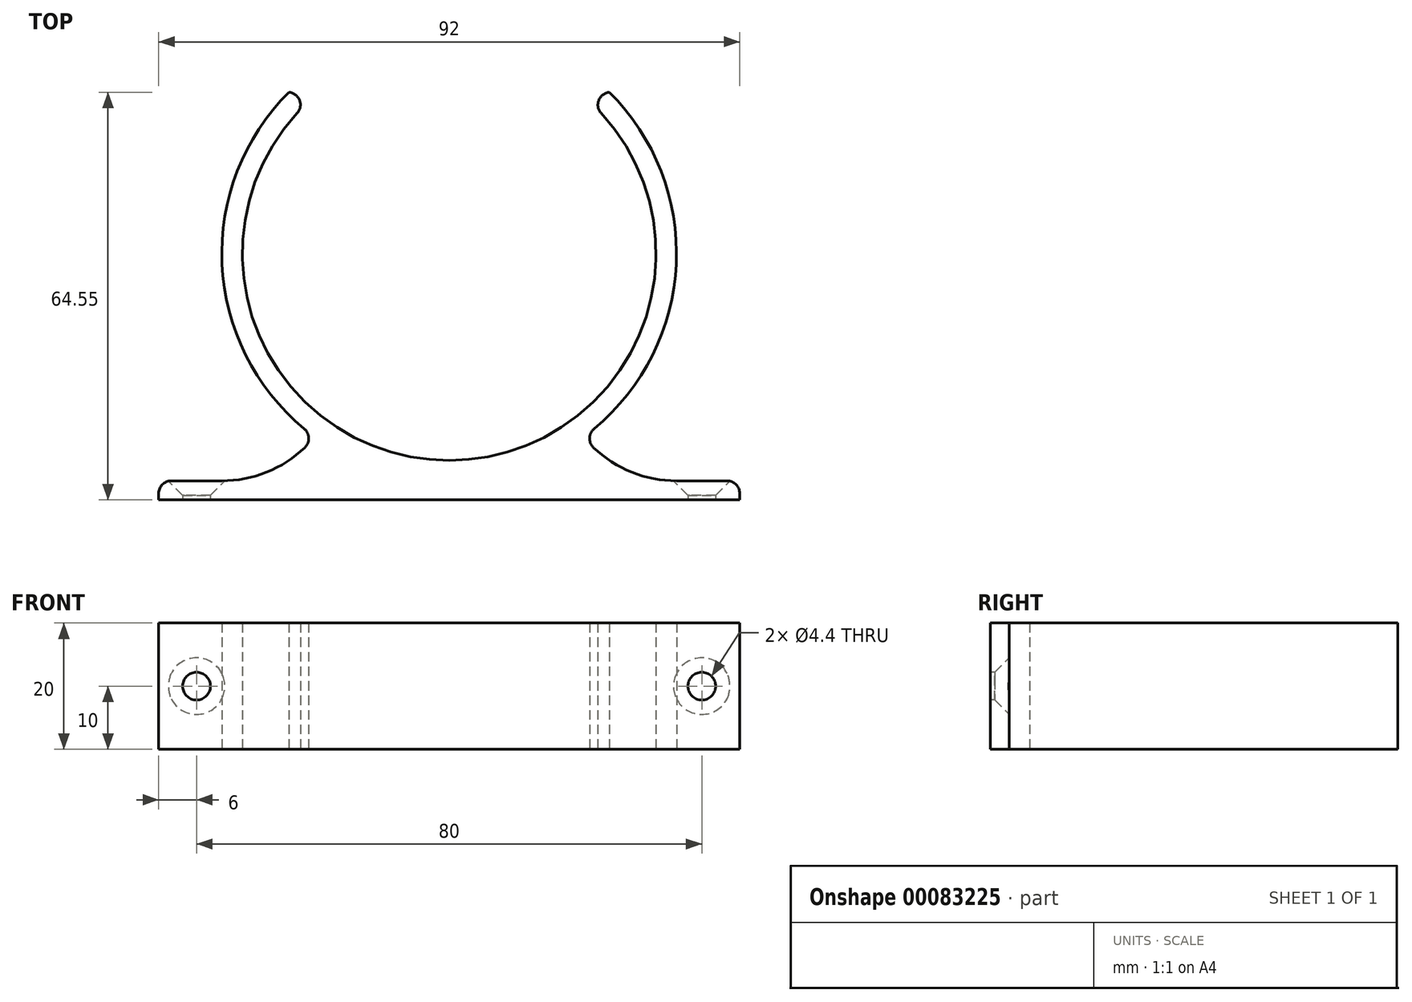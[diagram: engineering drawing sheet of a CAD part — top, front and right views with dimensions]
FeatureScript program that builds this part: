
annotation { "Feature Type Name" : "Feature", "Feature Type Description" : "" }
export const myFeature = defineFeature(function(context is Context, id is Id, definition is map)
    precondition{}
    {
        {
            assignVariable(context, id + "F0", {"name" : "h", "anyValue" : 20});
        }
        {
            var Q0;
            Q0=qCreatedBy(makeId("Top.planeOp"),FACE);
            var sketch = newSketch(context, id + "F1", { "sketchPlane" : qUnion([Q0])});
            skCircle(sketch, "E0", {"center": v(0, 0) * mm, "radius": 36 * mm});
            skCircle(sketch, "E1", {"center": v(0, 0) * mm, "radius": 32.75 * mm});
            skLineSegment(sketch, "E2", {"start": v(-36, 0) * mm, "end": v(36, 0) * mm, "construction": true});
            skLineSegment(sketch, "E3", {"start": v(36, 0) * mm, "end": v(36, -39) * mm});
            skLineSegment(sketch, "E4", {"start": v(36, -39) * mm, "end": v(-36, -39) * mm});
            skLineSegment(sketch, "E5", {"start": v(-36, -39) * mm, "end": v(-36, 0) * mm});
            skLineSegment(sketch, "E6", {"start": v(-36, -39) * mm, "end": v(-46, -39) * mm});
            skLineSegment(sketch, "E7", {"start": v(-46, -39) * mm, "end": v(-46, -36) * mm});
            skLineSegment(sketch, "E8", {"start": v(-46, -36) * mm, "end": v(-36, -36) * mm});
            skLineSegment(sketch, "E9", {"start": v(36, -39) * mm, "end": v(46, -39) * mm});
            skLineSegment(sketch, "E10", {"start": v(46, -39) * mm, "end": v(46, -36) * mm});
            skLineSegment(sketch, "E11", {"start": v(46, -36) * mm, "end": v(36, -36) * mm});
            skLineSegment(sketch, "E12", {"start": v(-36, -17.01) * mm, "end": v(36, -17.01) * mm, "construction": true});
            skCircle(sketch, "E13", {"center": v(-36, -17.01) * mm, "radius": 18.99 * mm});
            skCircle(sketch, "E14", {"center": v(36, -17.01) * mm, "radius": 18.99 * mm});
            skLineSegment(sketch, "E15", {"start": v(-25.37, 25.55) * mm, "end": v(25.37, 25.55) * mm, "construction": true});
            skLineSegment(sketch, "E16", {"start": v(-25.37, 25.55) * mm, "end": v(-20.5, 25.55) * mm});
            skLineSegment(sketch, "E17", {"start": v(25.37, 25.55) * mm, "end": v(20.5, 25.55) * mm});
            skSolve(sketch);
        }
        {
            var Q0;
            {var subQ0=sQuery(id+"F1.wireOp",EDGE,"E6");Q0=makeQuery(id+"F1.imprint","IMPRINT",FACE,{"disambiguationData":[TD([[makeQuery(id+"F1.imprint","IMPRINT",EDGE,{"derivedFrom":subQ0}),-1.0]])]});}
            var Q1;
            {var subQ1=sQuery(id+"F1.wireOp",EDGE,"E4");Q1=makeQuery(id+"F1.imprint","IMPRINT",FACE,{"disambiguationData":[TD([[makeQuery(id+"F1.imprint","IMPRINT",EDGE,{"derivedFrom":subQ1}),-1.0]])]});}
            var Q2;
            {var subQ0=sQuery(id+"F1.wireOp",EDGE,"E9");Q2=makeQuery(id+"F1.imprint","IMPRINT",FACE,{"disambiguationData":[TD([[makeQuery(id+"F1.imprint","IMPRINT",EDGE,{"derivedFrom":subQ0}),1.0]])]});}
            var Q3;
            {var subQ0=sQuery(id+"F1.wireOp",EDGE,"E13");var subQ1=sQuery(id+"F1.wireOp",EDGE,"E0");var subQ2=makeQuery(id+"F1.imprint","INTERSECT",VERTEX,{"disambiguationData":[OD(1.0)],"derivedFrom":[subQ1,subQ0]});Q3=makeQuery(id+"F1.imprint","IMPRINT",FACE,{"disambiguationData":[TD([[makeQuery(id+"F1.imprint","IMPRINT",EDGE,{"disambiguationData":[TD([[subQ2,-1.0]])],"derivedFrom":subQ1}),1.0]])]});}
            var Q4;
            {var subQ0=sQuery(id+"F1.wireOp",EDGE,"E14");var subQ1=sQuery(id+"F1.wireOp",EDGE,"E0");var subQ2=makeQuery(id+"F1.imprint","INTERSECT",VERTEX,{"disambiguationData":[OD(0.0)],"derivedFrom":[subQ1,subQ0]});Q4=makeQuery(id+"F1.imprint","IMPRINT",FACE,{"disambiguationData":[TD([[makeQuery(id+"F1.imprint","IMPRINT",EDGE,{"disambiguationData":[TD([[subQ2,-1.0]])],"derivedFrom":subQ1}),1.0]])]});}
            var Q5;
            {var subQ5=sQuery(id+"F1.wireOp",EDGE,"E0");var subQ6=makeQuery(id+"F1.imprint","INTERSECT",VERTEX,{"derivedFrom":[subQ5,sQuery(id+"F1.wireOp",EDGE,"E3")]});Q5=makeQuery(id+"F1.imprint","IMPRINT",FACE,{"disambiguationData":[TD([[makeQuery(id+"F1.imprint","IMPRINT",EDGE,{"disambiguationData":[TD([[subQ6,-1.0]])],"derivedFrom":subQ5}),1.0]])]});}
            var Q6;
            {var subQ0=sQuery(id+"F1.wireOp",EDGE,"E13");var subQ1=sQuery(id+"F1.wireOp",EDGE,"E0");var subQ2=makeQuery(id+"F1.imprint","INTERSECT",VERTEX,{"disambiguationData":[OD(0.0)],"derivedFrom":[subQ1,subQ0]});Q6=makeQuery(id+"F1.imprint","IMPRINT",FACE,{"disambiguationData":[TD([[makeQuery(id+"F1.imprint","IMPRINT",EDGE,{"disambiguationData":[TD([[subQ2,-1.0]])],"derivedFrom":subQ1}),1.0]])]});}
            var Q7;
            {var subQ5=sQuery(id+"F1.wireOp",EDGE,"E16");Q7=makeQuery(id+"F1.imprint","IMPRINT",FACE,{"disambiguationData":[TD([[makeQuery(id+"F1.imprint","IMPRINT",EDGE,{"derivedFrom":subQ5}),-1.0]])]});}
            extrude(context, id + "F2", {"entities" : qUnion([Q0, Q1, Q2, Q3, Q4, Q5, Q6, Q7]), "depth" : (getVariable(context, 'h')) * mm});
        }
        {
            var Q0;
            Q0=makeQuery(id+"F2.opExtrude","SWEPT_EDGE",EDGE,{"disambiguationData":[OSD([sQuery(id+"F1.wireOp",EDGE,"E1"),sQuery(id+"F1.wireOp",EDGE,"E17")])]});
            var Q1;
            Q1=makeQuery(id+"F2.opExtrude","SWEPT_EDGE",EDGE,{"disambiguationData":[OSD([sQuery(id+"F1.wireOp",EDGE,"E1"),sQuery(id+"F1.wireOp",EDGE,"E16")])]});
            var Q2;
            Q2=makeQuery(id+"F2.opExtrude","SWEPT_EDGE",EDGE,{"disambiguationData":[OSD([sQuery(id+"F1.wireOp",EDGE,"E0"),sQuery(id+"F1.wireOp",EDGE,"E13")])]});
            var Q3;
            Q3=makeQuery(id+"F2.opExtrude","SWEPT_EDGE",EDGE,{"disambiguationData":[OSD([sQuery(id+"F1.wireOp",EDGE,"E0"),sQuery(id+"F1.wireOp",EDGE,"E14")])]});
            var Q4;
            Q4=makeQuery(id+"F2.opExtrude","SWEPT_EDGE",EDGE,{"disambiguationData":[OSD([sQuery(id+"F1.wireOp",EDGE,"E10"),sQuery(id+"F1.wireOp",EDGE,"E11")])]});
            var Q5;
            Q5=makeQuery(id+"F2.opExtrude","SWEPT_EDGE",EDGE,{"disambiguationData":[OSD([sQuery(id+"F1.wireOp",EDGE,"E7"),sQuery(id+"F1.wireOp",EDGE,"E8")])]});
            fillet(context, id + "F3", {"entities" : qUnion([Q0, Q1, Q2, Q3, Q4, Q5]), "radius" : 2 * mm, "tangentPropagation" : true, "allowEdgeOverflow" : false});
        }
        {
            var Q0;
            Q0=makeQuery(id+"F2.opExtrude","SWEPT_FACE",FACE,{"disambiguationData":[OSD([sQuery(id+"F1.wireOp",EDGE,"E11")])]});
            var sketch = newSketch(context, id + "F4", { "sketchPlane" : qUnion([Q0])});
            skLineSegment(sketch, "E18", {"start": v(-44, 10) * mm, "end": v(17, 10) * mm, "construction": true});
            skPoint(sketch, "E19", {"position": v(-40, 10) * mm});
            skPoint(sketch, "E20", {"position": v(40, 10) * mm});
            skSolve(sketch);
        }
        {
            var Q0;
            Q0=sQuery(id+"F4.wireOp",VERTEX,"E20");
            var Q1;
            Q1=sQuery(id+"F4.wireOp",VERTEX,"E19");
            var Q2;
            Q2=makeQuery(id+"F2.opExtrude","SWEPT_BODY",BODY,{"disambiguationData":[OSD([sQuery(id+"F1.wireOp",EDGE,"E0"),sQuery(id+"F1.wireOp",EDGE,"E1"),sQuery(id+"F1.wireOp",EDGE,"E4"),sQuery(id+"F1.wireOp",EDGE,"E6"),sQuery(id+"F1.wireOp",EDGE,"E7"),sQuery(id+"F1.wireOp",EDGE,"E8"),sQuery(id+"F1.wireOp",EDGE,"E9"),sQuery(id+"F1.wireOp",EDGE,"E10"),sQuery(id+"F1.wireOp",EDGE,"E11"),sQuery(id+"F1.wireOp",EDGE,"E13"),sQuery(id+"F1.wireOp",EDGE,"E14"),sQuery(id+"F1.wireOp",EDGE,"E16"),sQuery(id+"F1.wireOp",EDGE,"E17")])]});
            hole(context, id + "F5", {"style" : HoleStyle.C_SINK, "endStyle" : HoleEndStyle.BLIND, "standardTappedOrClearance" : lookupTablePath({ "standard" : "ISO", "fit" : "Normal", "size" : "M4", "type" : "Clearance" }), "standardBlindInLast" : lookupTablePath({ "fit" : "Standard", "standard" : "ISO", "size" : "M4", "type" : "Clearance" }), "holeDiameter" : 4.4 * mm, "cSinkDiameter" : 8.96 * mm, "cSinkAngle" : 90 * degree, "holeDepth" : 12 * mm, "locations" : qUnion([Q0, Q1]), "scope" : qUnion([Q2]), "startStyle" : HoleStartStyle.PART});
        }
    });
